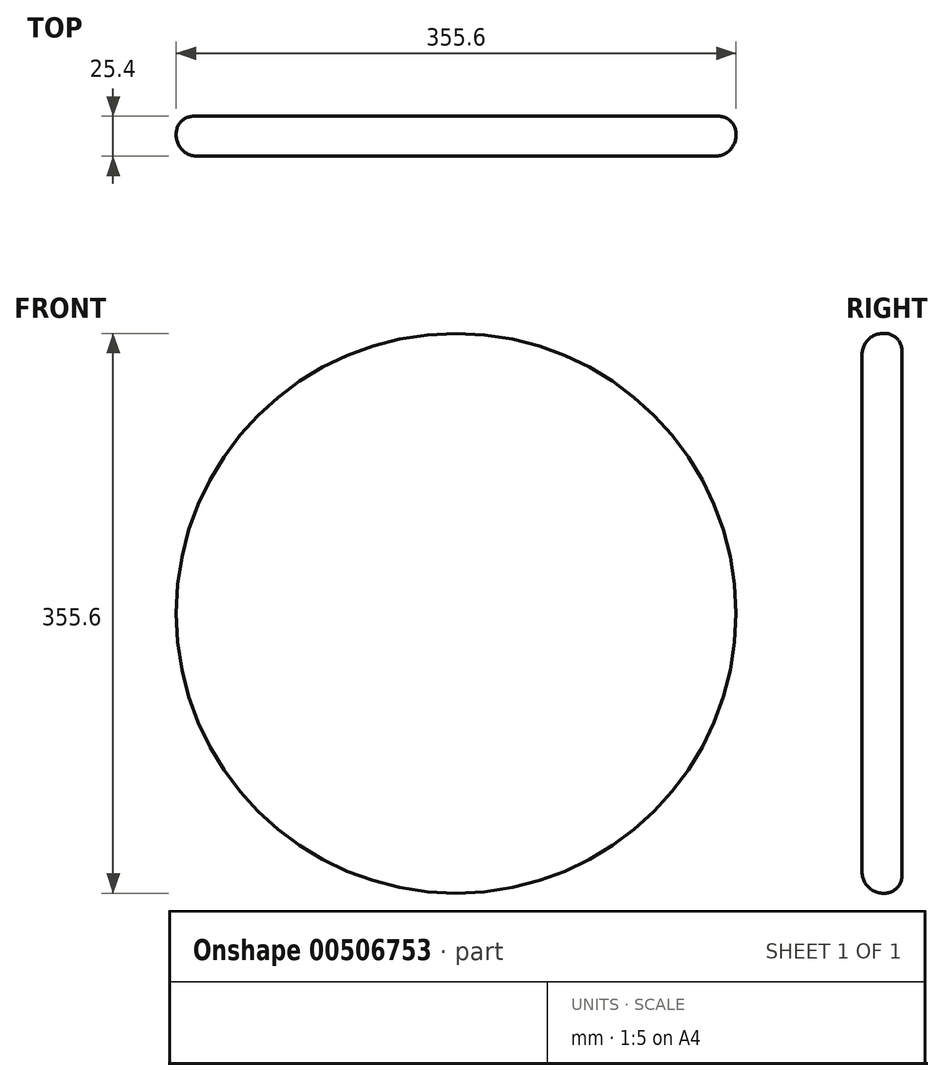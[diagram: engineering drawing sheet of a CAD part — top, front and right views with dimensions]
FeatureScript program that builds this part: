
annotation { "Feature Type Name" : "Feature", "Feature Type Description" : "" }
export const myFeature = defineFeature(function(context is Context, id is Id, definition is map)
    precondition{}
    {
        {
            var Q0;
            Q0=qCreatedBy(makeId("Front.planeOp"),FACE);
            var sketch = newSketch(context, id + "F0", { "sketchPlane" : qUnion([Q0])});
            skCircle(sketch, "E0", {"center": v(-8.81, -3.24) * mm, "radius": 177.8 * mm});
            skSolve(sketch);
        }
        {
            var Q0;
            Q0=makeQuery(id+"F0.imprint","IMPRINT",FACE,{"disambiguationData":[TD([[makeQuery(id+"F0.imprint","IMPRINT",EDGE,{"derivedFrom":sQuery(id+"F0.wireOp",EDGE,"E0")}),1.0]])]});
            extrude(context, id + "F1", {"entities" : qUnion([Q0]), "depth" : 25.4 * mm, "offsetDistance" : 25.4 * mm});
        }
        {
            var Q0;
            Q0=makeQuery(id+"F1.opExtrude","CAP_EDGE",EDGE,{"disambiguationData":[OSD([sQuery(id+"F0.wireOp",EDGE,"E0")])],"isStart":false});
            fillet(context, id + "F2", {"entities" : qUnion([Q0]), "radius" : 13.5 * mm, "tangentPropagation" : true, "allowEdgeOverflow" : false});
        }
        {
            var Q0;
            Q0=makeQuery(id+"F1.opExtrude","CAP_EDGE",EDGE,{"disambiguationData":[OSD([sQuery(id+"F0.wireOp",EDGE,"E0")])],"isStart":true});
            fillet(context, id + "F3", {"entities" : qUnion([Q0]), "radius" : 11.04 * mm, "tangentPropagation" : true, "allowEdgeOverflow" : false});
        }
    });
